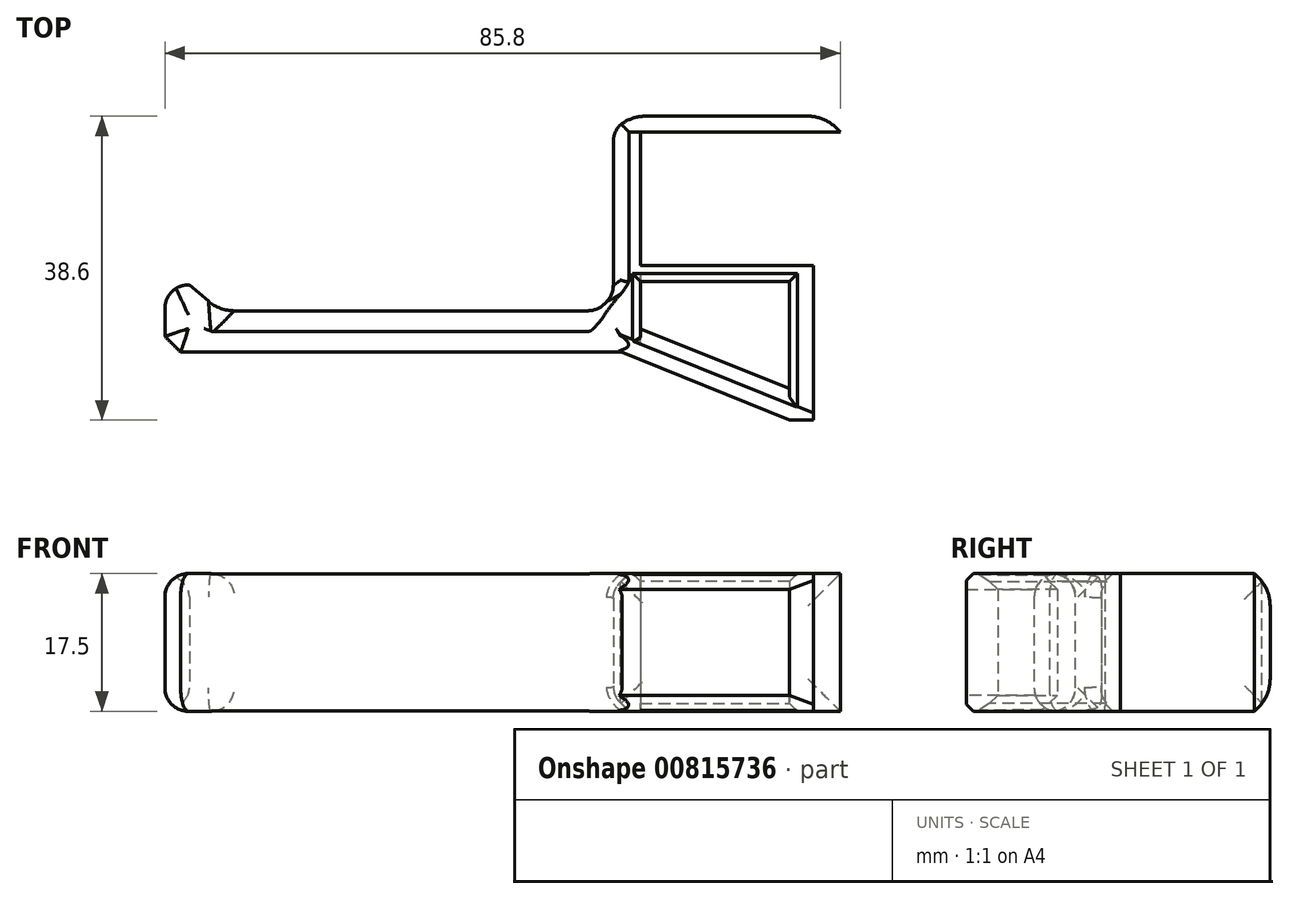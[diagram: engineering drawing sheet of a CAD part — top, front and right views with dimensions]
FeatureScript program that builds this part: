
annotation { "Feature Type Name" : "Feature", "Feature Type Description" : "" }
export const myFeature = defineFeature(function(context is Context, id is Id, definition is map)
    precondition{}
    {
        {
            var Q0;
            Q0=qCreatedBy(makeId("Top.planeOp"),FACE);
            var sketch = newSketch(context, id + "F0", { "sketchPlane" : qUnion([Q0])});
            skLineSegment(sketch, "E0", {"start": v(0, 0) * mm, "end": v(0, 17) * mm});
            skLineSegment(sketch, "E1", {"start": v(0, 17) * mm, "end": v(25.4, 17) * mm});
            skLineSegment(sketch, "E2", {"start": v(25.4, 17) * mm, "end": v(25.4, 19) * mm});
            skLineSegment(sketch, "E3", {"start": v(25.4, 19) * mm, "end": v(-3.44, 19) * mm});
            skLineSegment(sketch, "E4", {"start": v(0, 0) * mm, "end": v(22, 0) * mm});
            skLineSegment(sketch, "E5", {"start": v(22, 0) * mm, "end": v(22, -2) * mm});
            skLineSegment(sketch, "E6", {"start": v(22, -2) * mm, "end": v(0, -2) * mm});
            skLineSegment(sketch, "E7", {"start": v(22, -2) * mm, "end": v(22, -19.6) * mm});
            skLineSegment(sketch, "E8", {"start": v(22, -19.6) * mm, "end": v(18.96, -19.6) * mm});
            skLineSegment(sketch, "E9", {"start": v(18.96, -19.6) * mm, "end": v(18.96, -2) * mm});
            skLineSegment(sketch, "E10", {"start": v(-3.44, 19) * mm, "end": v(-3.44, -5.72) * mm});
            skLineSegment(sketch, "E11", {"start": v(-3.44, -5.72) * mm, "end": v(-53.44, -5.72) * mm});
            skLineSegment(sketch, "E12", {"start": v(-53.44, -5.72) * mm, "end": v(-57.28, -2.43) * mm});
            skLineSegment(sketch, "E13", {"start": v(-57.28, -2.43) * mm, "end": v(-60.4, -2.43) * mm});
            skLineSegment(sketch, "E14", {"start": v(-60.4, -2.43) * mm, "end": v(-60.4, -10.97) * mm});
            skLineSegment(sketch, "E15", {"start": v(-60.4, -10.97) * mm, "end": v(0, -10.97) * mm});
            skLineSegment(sketch, "E16", {"start": v(0, -10.97) * mm, "end": v(0, -2) * mm});
            skLineSegment(sketch, "E17", {"start": v(-2.32, -10.97) * mm, "end": v(18.96, -19.6) * mm});
            skLineSegment(sketch, "E18", {"start": v(0, -8.02) * mm, "end": v(18.96, -15.57) * mm});
            skSolve(sketch);
        }
        {
            var Q0;
            {var subQ0=sQuery(id+"F0.wireOp",EDGE,"E17");Q0=makeQuery(id+"F0.imprint","IMPRINT",FACE,{"disambiguationData":[TD([[makeQuery(id+"F0.imprint","IMPRINT",EDGE,{"derivedFrom":subQ0}),1.0]])]});}
            var Q1;
            {var subQ3=sQuery(id+"F0.wireOp",EDGE,"E7");Q1=makeQuery(id+"F0.imprint","IMPRINT",FACE,{"disambiguationData":[TD([[makeQuery(id+"F0.imprint","IMPRINT",EDGE,{"derivedFrom":subQ3}),-1.0]])]});}
            var Q2;
            Q2=makeQuery(id+"F0.imprint","IMPRINT",FACE,{"disambiguationData":[TD([[makeQuery(id+"F0.imprint","IMPRINT",EDGE,{"derivedFrom":sQuery(id+"F0.wireOp",EDGE,"E0")}),1.0]])]});
            extrude(context, id + "F1", {"entities" : qUnion([Q0, Q1, Q2]), "endBound" : BoundingType.SYMMETRIC, "depth" : 17.5 * mm, "offsetDistance" : 25.4 * mm});
        }
        {
            var Q0;
            Q0=makeQuery(id+"F1.opExtrude","CAP_EDGE",EDGE,{"disambiguationData":[OSD([sQuery(id+"F0.wireOp",EDGE,"E11")])],"isStart":false});
            var Q1;
            Q1=makeQuery(id+"F1.opExtrude","CAP_EDGE",EDGE,{"disambiguationData":[OSD([sQuery(id+"F0.wireOp",EDGE,"E11")])],"isStart":true});
            var Q2;
            Q2=makeQuery(id+"F1.opExtrude","CAP_EDGE",EDGE,{"disambiguationData":[OSD([sQuery(id+"F0.wireOp",EDGE,"E15")])],"isStart":false});
            var Q3;
            Q3=makeQuery(id+"F1.opExtrude","CAP_EDGE",EDGE,{"disambiguationData":[OSD([sQuery(id+"F0.wireOp",EDGE,"E15")])],"isStart":true});
            var Q4;
            Q4=makeQuery(id+"F1.opExtrude","CAP_EDGE",EDGE,{"disambiguationData":[OSD([sQuery(id+"F0.wireOp",EDGE,"E12")])],"isStart":false});
            var Q5;
            Q5=makeQuery(id+"F1.opExtrude","CAP_EDGE",EDGE,{"disambiguationData":[OSD([sQuery(id+"F0.wireOp",EDGE,"E12")])],"isStart":true});
            var Q6;
            Q6=makeQuery(id+"F1.opExtrude","SWEPT_EDGE",EDGE,{"disambiguationData":[OSD([sQuery(id+"F0.wireOp",EDGE,"E13"),sQuery(id+"F0.wireOp",EDGE,"E14")])]});
            var Q7;
            Q7=makeQuery(id+"F1.opExtrude","CAP_EDGE",EDGE,{"disambiguationData":[OSD([sQuery(id+"F0.wireOp",EDGE,"E14")])],"isStart":false});
            var Q8;
            Q8=makeQuery(id+"F1.opExtrude","CAP_EDGE",EDGE,{"disambiguationData":[OSD([sQuery(id+"F0.wireOp",EDGE,"E14")])],"isStart":true});
            fillet(context, id + "F2", {"entities" : qUnion([Q0, Q1, Q2, Q3, Q4, Q5, Q6, Q7, Q8]), "radius" : 3 * mm, "tangentPropagation" : true, "allowEdgeOverflow" : false});
        }
        {
            var Q0;
            Q0=makeQuery(id+"F1.opExtrude","CAP_EDGE",EDGE,{"disambiguationData":[OSD([sQuery(id+"F0.wireOp",EDGE,"E10")])],"isStart":false});
            var Q1;
            Q1=makeQuery(id+"F1.opExtrude","CAP_EDGE",EDGE,{"disambiguationData":[OSD([sQuery(id+"F0.wireOp",EDGE,"E10")])],"isStart":true});
            var Q2;
            Q2=makeQuery(id+"F1.opExtrude","CAP_EDGE",EDGE,{"disambiguationData":[OSD([sQuery(id+"F0.wireOp",EDGE,"E18")])],"isStart":false});
            var Q3;
            Q3=makeQuery(id+"F1.opExtrude","CAP_EDGE",EDGE,{"disambiguationData":[OSD([sQuery(id+"F0.wireOp",EDGE,"E18")])],"isStart":true});
            chamfer(context, id + "F3", {"entities" : qUnion([Q0, Q1, Q2, Q3]), "width" : 2 * mm, "tangentPropagation" : true});
        }
        {
            var Q0;
            Q0=makeQuery(id+"F1.opExtrude","CAP_EDGE",EDGE,{"disambiguationData":[OSD([sQuery(id+"F0.wireOp",EDGE,"E17")])],"isStart":true});
            var Q1;
            Q1=makeQuery(id+"F1.opExtrude","CAP_EDGE",EDGE,{"disambiguationData":[OSD([sQuery(id+"F0.wireOp",EDGE,"E17")])],"isStart":false});
            chamfer(context, id + "F4", {"entities" : qUnion([Q0, Q1]), "width" : 2 * mm, "tangentPropagation" : true});
        }
        {
            var Q0;
            Q0=makeQuery(id+"F1.opExtrude","CAP_EDGE",EDGE,{"disambiguationData":[OSD([sQuery(id+"F0.wireOp",EDGE,"E9")])],"isStart":true});
            var Q1;
            Q1=makeQuery(id+"F1.opExtrude","CAP_EDGE",EDGE,{"disambiguationData":[OSD([sQuery(id+"F0.wireOp",EDGE,"E9")])],"isStart":false});
            var Q2;
            Q2=makeQuery(id+"F1.opExtrude","CAP_EDGE",EDGE,{"disambiguationData":[OSD([sQuery(id+"F0.wireOp",EDGE,"E16")])],"isStart":false});
            chamfer(context, id + "F5", {"entities" : qUnion([Q0, Q1, Q2]), "width" : 1 * mm, "tangentPropagation" : true});
        }
        {
            var Q0;
            Q0=makeQuery(id+"F1.opExtrude","CAP_EDGE",EDGE,{"disambiguationData":[OSD([sQuery(id+"F0.wireOp",EDGE,"E6")])],"isStart":false});
            var Q1;
            Q1=makeQuery(id+"F1.opExtrude","CAP_EDGE",EDGE,{"disambiguationData":[OSD([sQuery(id+"F0.wireOp",EDGE,"E6")])],"isStart":true});
            chamfer(context, id + "F6", {"entities" : qUnion([Q0, Q1]), "width" : 1 * mm, "tangentPropagation" : true});
        }
        {
            var Q0;
            Q0=makeQuery(id+"F1.opExtrude","SWEPT_EDGE",EDGE,{"disambiguationData":[OSD([sQuery(id+"F0.wireOp",EDGE,"E3"),sQuery(id+"F0.wireOp",EDGE,"E10")])]});
            chamfer(context, id + "F7", {"entities" : qUnion([Q0]), "width" : 2 * mm, "tangentPropagation" : true});
        }
        {
            var Q0;
            Q0=makeQuery(id+"F1.opExtrude","SWEPT_EDGE",EDGE,{"disambiguationData":[OSD([sQuery(id+"F0.wireOp",EDGE,"E10"),sQuery(id+"F0.wireOp",EDGE,"E11")])]});
            chamfer(context, id + "F8", {"entities" : qUnion([Q0]), "width" : 2 * mm, "tangentPropagation" : true});
        }
        {
            var Q0;
            Q0=makeQuery(id+"F1.opExtrude","CAP_EDGE",EDGE,{"disambiguationData":[OSD([sQuery(id+"F0.wireOp",EDGE,"E3")])],"isStart":false});
            var Q1;
            Q1=makeQuery(id+"F1.opExtrude","CAP_EDGE",EDGE,{"disambiguationData":[OSD([sQuery(id+"F0.wireOp",EDGE,"E3")])],"isStart":true});
            var Q2;
            Q2=makeQuery(id+"F1.opExtrude","SWEPT_EDGE",EDGE,{"disambiguationData":[OSD([sQuery(id+"F0.wireOp",EDGE,"E2"),sQuery(id+"F0.wireOp",EDGE,"E3")])]});
            chamfer(context, id + "F9", {"entities" : qUnion([Q0, Q1, Q2]), "width" : 2 * mm, "tangentPropagation" : true});
        }
        {
            var Q0;
            Q0=makeQuery(id+"F1.opExtrude","SWEPT_EDGE",EDGE,{"disambiguationData":[OSD([sQuery(id+"F0.wireOp",EDGE,"E14"),sQuery(id+"F0.wireOp",EDGE,"E15")])]});
            chamfer(context, id + "F10", {"entities" : qUnion([Q0]), "width" : 2 * mm, "tangentPropagation" : true});
        }
        {
            var Q0;
            Q0=makeQuery(id+"F1.opExtrude","SWEPT_EDGE",EDGE,{"disambiguationData":[OSD([sQuery(id+"F0.wireOp",EDGE,"E11"),sQuery(id+"F0.wireOp",EDGE,"E12")])]});
            fillet(context, id + "F11", {"entities" : qUnion([Q0]), "radius" : 5.08 * mm, "tangentPropagation" : true, "allowEdgeOverflow" : false});
        }
        {
            var Q0;
            {var subQ0=sQuery(id+"F0.wireOp",EDGE,"E10");Q0=makeQuery(id+"F7.opChamfer","BLEND_EDGE",EDGE,{"blendedFrom":[makeQuery(id+"F1.opExtrude","SWEPT_EDGE",EDGE,{"disambiguationData":[OSD([sQuery(id+"F0.wireOp",EDGE,"E3"),subQ0])]}),makeQuery(id+"F1.opExtrude","SWEPT_FACE",FACE,{"disambiguationData":[OSD([subQ0])]})],"blendedInto":[makeQuery(id+"F1.opExtrude","SWEPT_FACE",FACE,{"disambiguationData":[OSD([subQ0])]})]});}
            var Q1;
            {var subQ0=sQuery(id+"F0.wireOp",EDGE,"E10");Q1=makeQuery(id+"F3.opChamfer","BLEND_EDGE",EDGE,{"blendedFrom":[makeQuery(id+"F1.opExtrude","CAP_EDGE",EDGE,{"disambiguationData":[OSD([subQ0])],"isStart":false}),makeQuery(id+"F1.opExtrude","SWEPT_FACE",FACE,{"disambiguationData":[OSD([subQ0])]})],"blendedInto":[makeQuery(id+"F1.opExtrude","SWEPT_FACE",FACE,{"disambiguationData":[OSD([subQ0])]})]});}
            var Q2;
            {var subQ0=sQuery(id+"F0.wireOp",EDGE,"E10");Q2=makeQuery(id+"F3.opChamfer","BLEND_EDGE",EDGE,{"blendedFrom":[makeQuery(id+"F1.opExtrude","CAP_EDGE",EDGE,{"disambiguationData":[OSD([subQ0])],"isStart":true}),makeQuery(id+"F1.opExtrude","SWEPT_FACE",FACE,{"disambiguationData":[OSD([subQ0])]})],"blendedInto":[makeQuery(id+"F1.opExtrude","SWEPT_FACE",FACE,{"disambiguationData":[OSD([subQ0])]})]});}
            var Q3;
            {var subQ0=sQuery(id+"F0.wireOp",EDGE,"E10");Q3=makeQuery(id+"F8.opChamfer","BLEND_EDGE",EDGE,{"disambiguationData":[OD(2.0)],"blendedFrom":[makeQuery(id+"F1.opExtrude","SWEPT_EDGE",EDGE,{"disambiguationData":[OSD([subQ0,sQuery(id+"F0.wireOp",EDGE,"E11")])]}),makeQuery(id+"F1.opExtrude","SWEPT_FACE",FACE,{"disambiguationData":[OSD([subQ0])]})],"blendedInto":[makeQuery(id+"F1.opExtrude","SWEPT_FACE",FACE,{"disambiguationData":[OSD([subQ0])]})]});}
            var Q4;
            {var subQ0=sQuery(id+"F0.wireOp",EDGE,"E11");Q4=makeQuery(id+"F8.opChamfer","BLEND_EDGE",EDGE,{"blendedFrom":[makeQuery(id+"F1.opExtrude","SWEPT_EDGE",EDGE,{"disambiguationData":[OSD([sQuery(id+"F0.wireOp",EDGE,"E10"),subQ0])]}),makeQuery(id+"F1.opExtrude","SWEPT_FACE",FACE,{"disambiguationData":[OSD([subQ0])]})],"blendedInto":[makeQuery(id+"F1.opExtrude","SWEPT_FACE",FACE,{"disambiguationData":[OSD([subQ0])]})]});}
            fillet(context, id + "F12", {"entities" : qUnion([Q0, Q1, Q2, Q3, Q4]), "radius" : 3 * mm, "tangentPropagation" : true, "allowEdgeOverflow" : false});
        }
        {
            var Q0;
            {var subQ0=sQuery(id+"F0.wireOp",EDGE,"E3");Q0=makeQuery(id+"F7.opChamfer","BLEND_EDGE",EDGE,{"blendedFrom":[makeQuery(id+"F1.opExtrude","SWEPT_EDGE",EDGE,{"disambiguationData":[OSD([subQ0,sQuery(id+"F0.wireOp",EDGE,"E10")])]}),makeQuery(id+"F1.opExtrude","SWEPT_FACE",FACE,{"disambiguationData":[OSD([subQ0])]})],"blendedInto":[makeQuery(id+"F1.opExtrude","SWEPT_FACE",FACE,{"disambiguationData":[OSD([subQ0])]})]});}
            var Q1;
            {var subQ0=sQuery(id+"F0.wireOp",EDGE,"E3");Q1=makeQuery(id+"F9.opChamfer","BLEND_EDGE",EDGE,{"blendedFrom":[makeQuery(id+"F1.opExtrude","CAP_EDGE",EDGE,{"disambiguationData":[OSD([subQ0])],"isStart":true}),makeQuery(id+"F1.opExtrude","SWEPT_FACE",FACE,{"disambiguationData":[OSD([subQ0])]})],"blendedInto":[makeQuery(id+"F1.opExtrude","SWEPT_FACE",FACE,{"disambiguationData":[OSD([subQ0])]})]});}
            var Q2;
            {var subQ0=sQuery(id+"F0.wireOp",EDGE,"E3");Q2=makeQuery(id+"F9.opChamfer","BLEND_EDGE",EDGE,{"blendedFrom":[makeQuery(id+"F1.opExtrude","CAP_EDGE",EDGE,{"disambiguationData":[OSD([subQ0])],"isStart":false}),makeQuery(id+"F1.opExtrude","SWEPT_FACE",FACE,{"disambiguationData":[OSD([subQ0])]})],"blendedInto":[makeQuery(id+"F1.opExtrude","SWEPT_FACE",FACE,{"disambiguationData":[OSD([subQ0])]})]});}
            var Q3;
            {var subQ0=sQuery(id+"F0.wireOp",EDGE,"E3");Q3=makeQuery(id+"F9.opChamfer","BLEND_EDGE",EDGE,{"blendedFrom":[makeQuery(id+"F1.opExtrude","SWEPT_EDGE",EDGE,{"disambiguationData":[OSD([sQuery(id+"F0.wireOp",EDGE,"E2"),subQ0])]}),makeQuery(id+"F1.opExtrude","SWEPT_FACE",FACE,{"disambiguationData":[OSD([subQ0])]})],"blendedInto":[makeQuery(id+"F1.opExtrude","SWEPT_FACE",FACE,{"disambiguationData":[OSD([subQ0])]})]});}
            fillet(context, id + "F13", {"entities" : qUnion([Q0, Q1, Q2, Q3]), "radius" : 5.08 * mm, "tangentPropagation" : true, "allowEdgeOverflow" : false});
        }
    });
